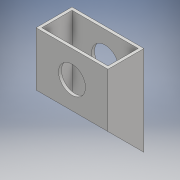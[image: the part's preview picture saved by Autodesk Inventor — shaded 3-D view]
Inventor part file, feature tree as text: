
AUTODESK INVENTOR PART (.ipt)
format: ipt  version: 2018 (Build 220112000, 112)  size: 117,248 bytes
history: native  units: mm
features: sketch x2, other x1, extrude x1, chamfer x1, hole x1
ambient origin geometry x8: Origin, YZ Plane, XZ Plane, XY Plane, X Axis, Y Axis, Z Axis, Center Point
bodies: Body1 (feature_tree)
feature tree (6):
  other  "ソリッド1"
  extrude  "押し出し1"  Depth=40.0mm
  chamfer  "面取り1"  Distance=20.0mm
  hole  "穴1"  [1 undecoded]
  sketch  "スケッチ1"
  sketch  "スケッチ2"
note: 1 required parameter value undecoded (feature->parameter linkage not recoverable at this tier; creation-order binding heuristic only, values carry confidence <= 0.55)
